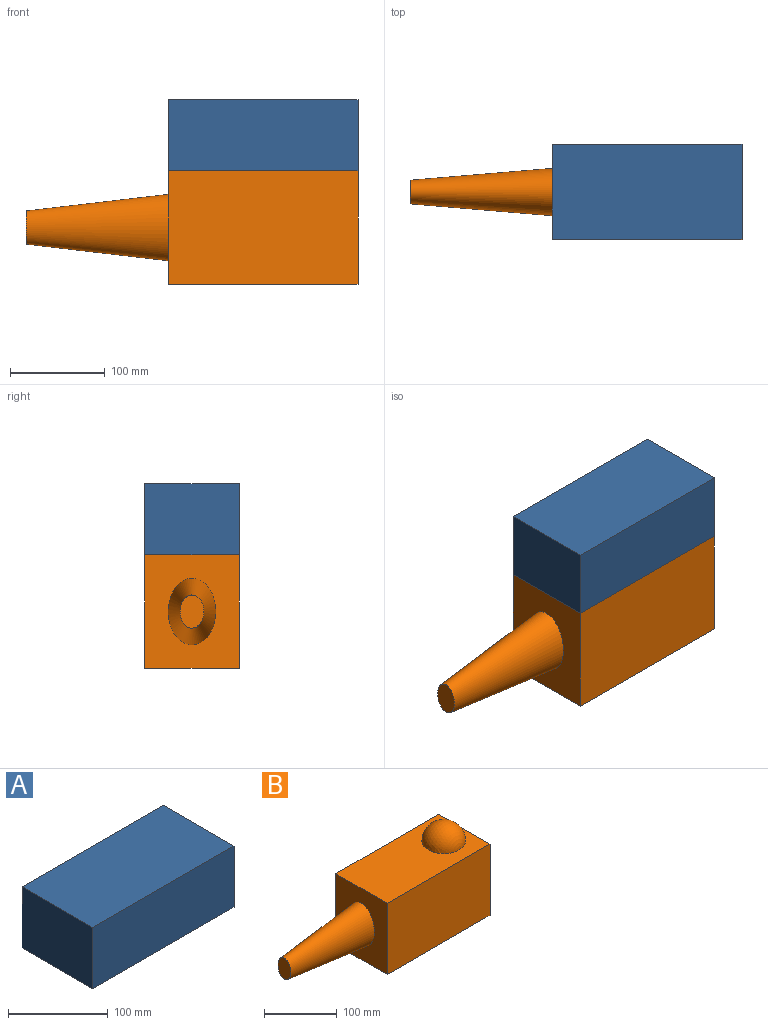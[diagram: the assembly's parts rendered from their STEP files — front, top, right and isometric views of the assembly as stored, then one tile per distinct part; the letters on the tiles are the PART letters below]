
ASSEMBLY  parts=2 mates=1
PART A: 7 faces, bbox 200x100x75 mm
  f0: plane 200x75mm, normal (0,-1,0), area 15000mm2, adj f1,f3,f4,f5
  f1: plane 100x75mm, normal (1,0,0), area 7500mm2, adj f0,f2,f4,f5
  f2: plane 200x75mm, normal (0,1,0), area 15000mm2, adj f1,f3,f4,f5
  f3: plane 100x75mm, normal (-1,0,0), area 7500mm2, adj f0,f2,f4,f5
  f4: plane 200x100mm, normal (0,0,1), area 20000mm2, adj f0,f1,f2,f3
  f5: plane 200x100mm, normal (0,0,-1), area 18743.4mm2, adj f0,f1,f2,f3,f6
  f6: sphere r=20mm, area 2513.3mm2, adj f5
PART B: 9 faces, bbox 350x100x150 mm
  f0: plane 120x100mm, normal (-1,0,0), area 9251.4mm2, adj f1,f3,f4,f5,f8
  f1: plane 200x120mm, normal (0,-1,0), area 24000mm2, adj f0,f2,f4,f5
  f2: plane 120x100mm, normal (1,0,0), area 12000mm2, adj f1,f3,f4,f5
  f3: plane 200x120mm, normal (0,1,0), area 24000mm2, adj f0,f2,f4,f5
  f4: plane 200x100mm, normal (0,0,1), area 17172.6mm2, adj f0,f1,f2,f3,f6
  f5: plane 200x100mm, normal (0,0,-1), area 20000mm2, adj f0,f1,f2,f3
  f6: sphere r=30mm, area 5654.9mm2, adj f4
  f7: plane 35x25mm, normal (-1,0,0), area 687.1mm2, adj f8
  f8: bspline ~150x70mm, area 21453.9mm2, adj f0,f7
PLACE A t=(-39.47,30.11,47.06)mm
PLACE B t=(-39.47,30.11,-72.94)mm
MATE fastened B.f4 <-> A.f5  axis (0,0,1) through (20.53,30.11,47.06)mm
